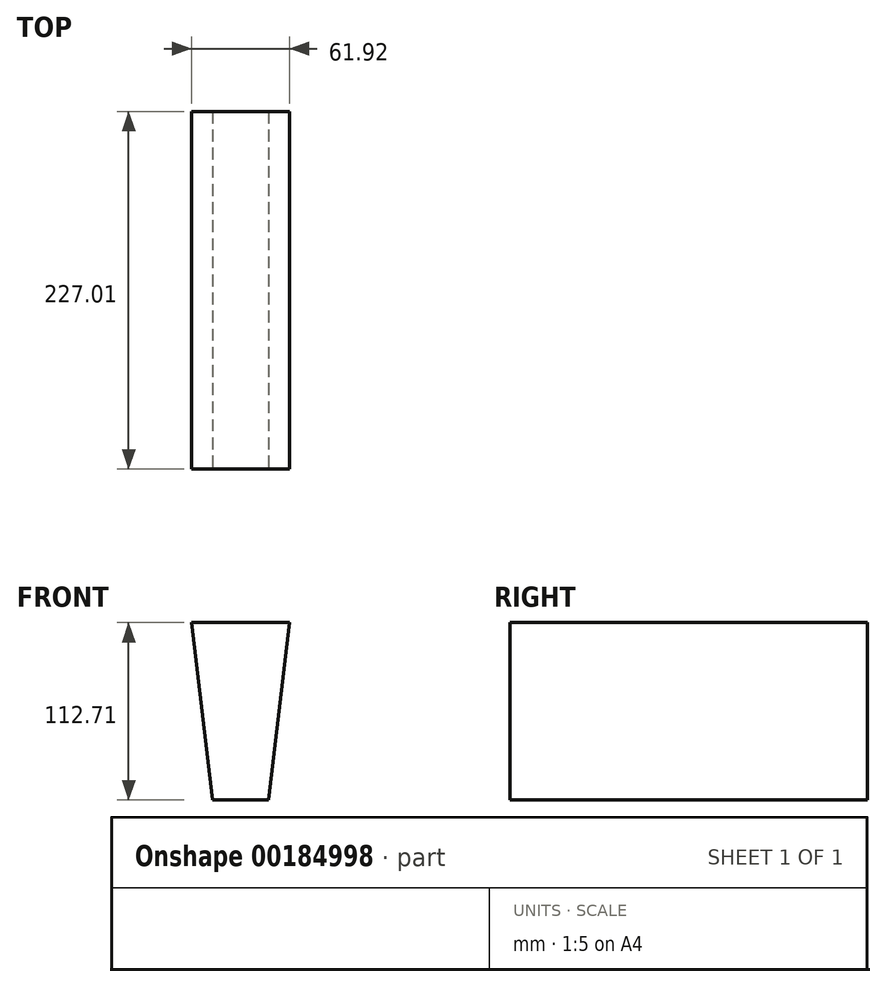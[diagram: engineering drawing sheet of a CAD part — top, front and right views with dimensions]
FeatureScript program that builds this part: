
annotation { "Feature Type Name" : "Feature", "Feature Type Description" : "" }
export const myFeature = defineFeature(function(context is Context, id is Id, definition is map)
    precondition{}
    {
        {
            var Q0;
            Q0=qCreatedBy(makeId("Front.planeOp"),FACE);
            var sketch = newSketch(context, id + "F0", { "sketchPlane" : qUnion([Q0])});
            skLineSegment(sketch, "E0.bottom", {"start": v(-30.96, 328.61) * mm, "end": v(30.96, 328.61) * mm});
            skLineSegment(sketch, "E0.top", {"start": v(-17.87, 215.9) * mm, "end": v(17.87, 215.9) * mm});
            skLineSegment(sketch, "E1.MirrorCS", {"start": v(17.87, 215.9) * mm, "end": v(30.96, 328.61) * mm});
            skLineSegment(sketch, "E2.MirrorCS", {"start": v(-17.87, 215.9) * mm, "end": v(-30.96, 328.61) * mm});
            skLineSegment(sketch, "E3", {"start": v(0, 0) * mm, "end": v(0, 328.61) * mm, "construction": true});
            skPoint(sketch, "E4", {"position": v(0, 61.91) * mm});
            skSolve(sketch);
        }
        {
            var Q0;
            Q0=makeQuery(id+"F0.imprint","IMPRINT",FACE,{"disambiguationData":[TD([[makeQuery(id+"F0.imprint","IMPRINT",EDGE,{"derivedFrom":sQuery(id+"F0.wireOp",EDGE,"E0.bottom")}),-1.0]])]});
            extrude(context, id + "F1", {"entities" : qUnion([Q0]), "oppositeDirection" : true, "depth" : 227 * mm});
        }
    });
